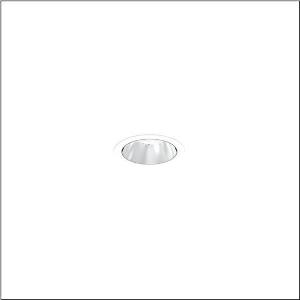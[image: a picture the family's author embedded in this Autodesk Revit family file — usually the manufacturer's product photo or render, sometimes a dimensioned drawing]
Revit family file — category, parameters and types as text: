
# Revit family: lunis_21_s_51db15ma91c
name_source: partatom
category: Lighting Fixtures
units: mm (PartAtom-declared; Revit-internal decimal feet)

## family parameters
Cut with Voids When Loaded = No
Host = Face
Light Source = No
Part Type = Normal
Room Calculation Point = No
Round Connector Dimension = Use Diameter
Shared = No

## types (1)
- --- (1 x LED, 990 lm, 5.9 W, 4000K)
    Apparent Load = 6 VA
    CIE Flux Codes = 95 100 100 100 100
    Color Rendering = 80
    Color Temperature = 4000K
    Default Elevation = 1800 mm
    Description = Lunis 21,  S, downlight, light control with lens, of PMMA, anti glare with reflector, of PC, highly specular, light emission: direct distribution, LED rated luminous flux: 990lm, light colour: 830/840/865, with terminal, 3-pole, mains connection: 220..240V, AC, 50..60Hz, housing, round, of diecast aluminium, traffic white (RAL 9016), diameter: 84mm, clamping range: 1..40mm, protection rating (complete): IP20, protection rating (on room side): IP54, insulation class (complete): insulation class II (safety insulation), certification: CE, impact resistance: IK03, packaging unit: 1 piece
    Height = 0 mm  [stored 0 ft]
    Lamp = 1 x LED
    Lamp Light Flux = 990 lm
    Lamp Power = 5.9 W
    Lamp count = 1
    Length = 84 mm
    Luminous efficacy = 168 lm/W
    Manufacturer = Siteco
    ModVariant = No
    Model = 51DB15MA91C
    Mounting Place = Ceiling
    Mounting Type = Recessed
    Number of Poles = 1
    OnlyDefault = Yes
    Power Factor = 1
    Product Name = Lunis 21 S
    Product group = downlight
    ProductGroupID = 400
    Protection Class = Protection class II
    Protection Degree = IP 20
    RLX_Detail_Level = 1
    RLX_Emergency_Light_Flux = 0 lm
    RLX_Emergency_Type = 0
    RLX_Emergency_Type_DB = No
    RlxData = <blob elided: 7945 chars, md5=3d00b954>
    Socket = socket
    Standby Power = 0 W
    System Light Flux = 990 lm
    System Power = 6 W
    Type Comments = factory setting: colour temperature 4000K
    Type Image = l_1290840.jpg
    URL = http://relux.com
    VarID = @adj_017539
    Voltage = 0 V
    Weight = 0.00 kg
    Width = 0 mm  [stored 0 ft]

note: [stored X ft] marks values corroborated as IEEE doubles in the binary element streams (Revit-internal decimal feet)

## geometry (parser evidence)
native form markers: Sweep x9
no freeform markers — native parametric forms only
